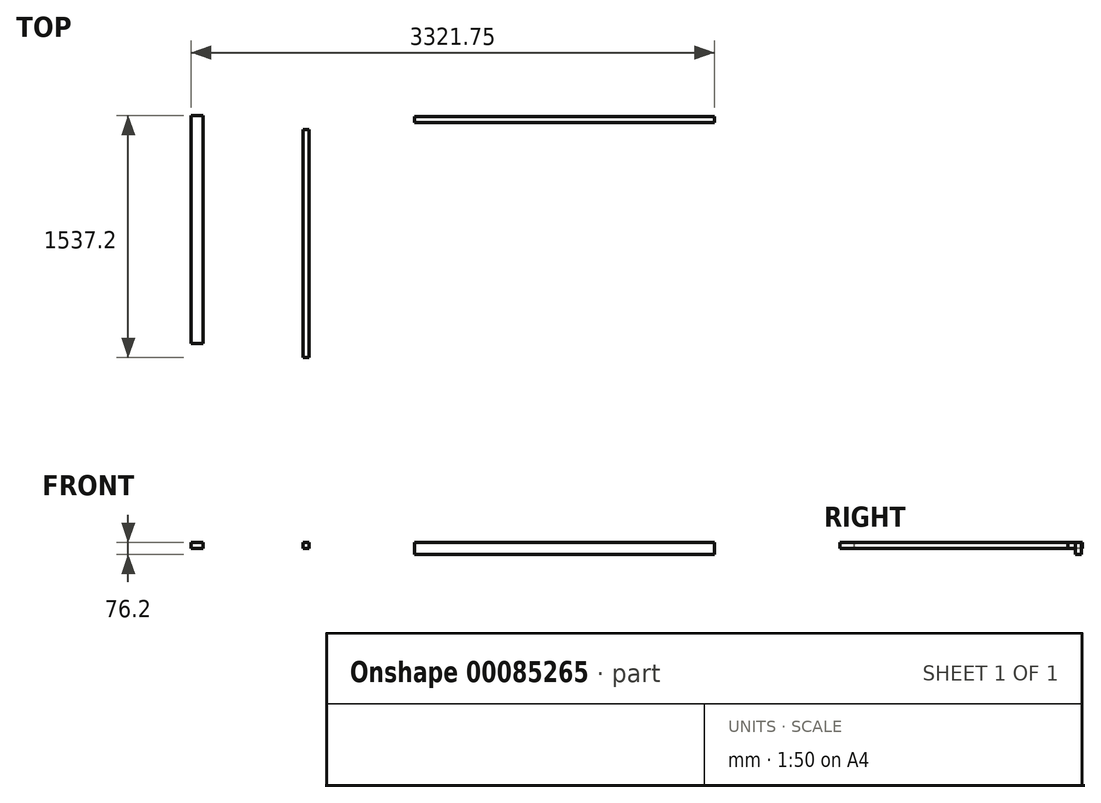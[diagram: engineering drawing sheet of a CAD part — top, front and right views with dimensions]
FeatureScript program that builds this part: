
annotation { "Feature Type Name" : "Feature", "Feature Type Description" : "" }
export const myFeature = defineFeature(function(context is Context, id is Id, definition is map)
    precondition{}
    {
        {
            var Q0;
            Q0=qCreatedBy(makeId("Top.planeOp"),FACE);
            var sketch = newSketch(context, id + "F0", { "sketchPlane" : qUnion([Q0])});
            skLineSegment(sketch, "E0.bottom", {"start": v(-1059.73, 354) * mm, "end": v(845.27, 354) * mm});
            skLineSegment(sketch, "E0.top", {"start": v(-1059.73, 315.9) * mm, "end": v(845.27, 315.9) * mm});
            skLineSegment(sketch, "E0.left", {"start": v(-1059.73, 354) * mm, "end": v(-1059.73, 315.9) * mm});
            skLineSegment(sketch, "E0.right", {"start": v(845.27, 354) * mm, "end": v(845.27, 315.9) * mm});
            skSolve(sketch);
        }
        {
            var Q0;
            Q0=makeQuery(id+"F0.imprint","IMPRINT",FACE,{"disambiguationData":[TD([[makeQuery(id+"F0.imprint","IMPRINT",EDGE,{"derivedFrom":sQuery(id+"F0.wireOp",EDGE,"E0.bottom")}),-1.0]])]});
            var Q1;
            Q1=sQuery(id+"F0.wireOp",EDGE,"E0.top");
            var Q2;
            Q2=sQuery(id+"F0.wireOp",EDGE,"E0.bottom");
            var Q3;
            Q3=sQuery(id+"F0.wireOp",EDGE,"E0.left");
            var Q4;
            Q4=sQuery(id+"F0.wireOp",EDGE,"E0.right");
            extrude(context, id + "F1", {"entities" : qUnion([Q0]), "surfaceEntities" : qUnion([Q1, Q2, Q3, Q4]), "oppositeDirection" : true, "depth" : 76.2 * mm});
        }
        {
            var Q0;
            Q0=qCreatedBy(makeId("Top.planeOp"),FACE);
            var sketch = newSketch(context, id + "F2", { "sketchPlane" : qUnion([Q0])});
            skLineSegment(sketch, "E1.bottom", {"start": v(-2476.48, 359.9) * mm, "end": v(-2400.28, 359.9) * mm});
            skLineSegment(sketch, "E1.top", {"start": v(-2476.48, -1087.9) * mm, "end": v(-2400.28, -1087.9) * mm});
            skLineSegment(sketch, "E1.left", {"start": v(-2476.48, 359.9) * mm, "end": v(-2476.48, -1087.9) * mm});
            skLineSegment(sketch, "E1.right", {"start": v(-2400.28, 359.9) * mm, "end": v(-2400.28, -1087.9) * mm});
            skSolve(sketch);
        }
        {
            var Q0;
            Q0=makeQuery(id+"F2.imprint","IMPRINT",FACE,{"disambiguationData":[TD([[makeQuery(id+"F2.imprint","IMPRINT",EDGE,{"derivedFrom":sQuery(id+"F2.wireOp",EDGE,"E1.bottom")}),-1.0]])]});
            var Q1;
            Q1=sQuery(id+"F2.wireOp",EDGE,"E1.right");
            var Q2;
            Q2=sQuery(id+"F2.wireOp",EDGE,"E1.left");
            var Q3;
            Q3=sQuery(id+"F2.wireOp",EDGE,"E1.top");
            var Q4;
            Q4=sQuery(id+"F2.wireOp",EDGE,"E1.bottom");
            extrude(context, id + "F3", {"entities" : qUnion([Q0]), "surfaceEntities" : qUnion([Q1, Q2, Q3, Q4]), "oppositeDirection" : true, "depth" : 38.1 * mm});
        }
        {
            var Q0;
            Q0=qCreatedBy(makeId("Top.planeOp"),FACE);
            var sketch = newSketch(context, id + "F4", { "sketchPlane" : qUnion([Q0])});
            skLineSegment(sketch, "E2.bottom", {"start": v(-1764.69, 270.5) * mm, "end": v(-1726.59, 270.5) * mm});
            skLineSegment(sketch, "E2.top", {"start": v(-1764.69, -1177.3) * mm, "end": v(-1726.59, -1177.3) * mm});
            skLineSegment(sketch, "E2.left", {"start": v(-1764.69, 270.5) * mm, "end": v(-1764.69, -1177.3) * mm});
            skLineSegment(sketch, "E2.right", {"start": v(-1726.59, 270.5) * mm, "end": v(-1726.59, -1177.3) * mm});
            skSolve(sketch);
        }
        {
            var Q0;
            Q0=makeQuery(id+"F4.imprint","IMPRINT",FACE,{"disambiguationData":[TD([[makeQuery(id+"F4.imprint","IMPRINT",EDGE,{"derivedFrom":sQuery(id+"F4.wireOp",EDGE,"E2.bottom")}),-1.0]])]});
            var Q1;
            Q1=sQuery(id+"F4.wireOp",EDGE,"E2.left");
            var Q2;
            Q2=sQuery(id+"F4.wireOp",EDGE,"E2.bottom");
            var Q3;
            Q3=sQuery(id+"F4.wireOp",EDGE,"E2.top");
            extrude(context, id + "F5", {"entities" : qUnion([Q0]), "surfaceEntities" : qUnion([Q1, Q2, Q3]), "oppositeDirection" : true, "depth" : 38.1 * mm});
        }
    });
